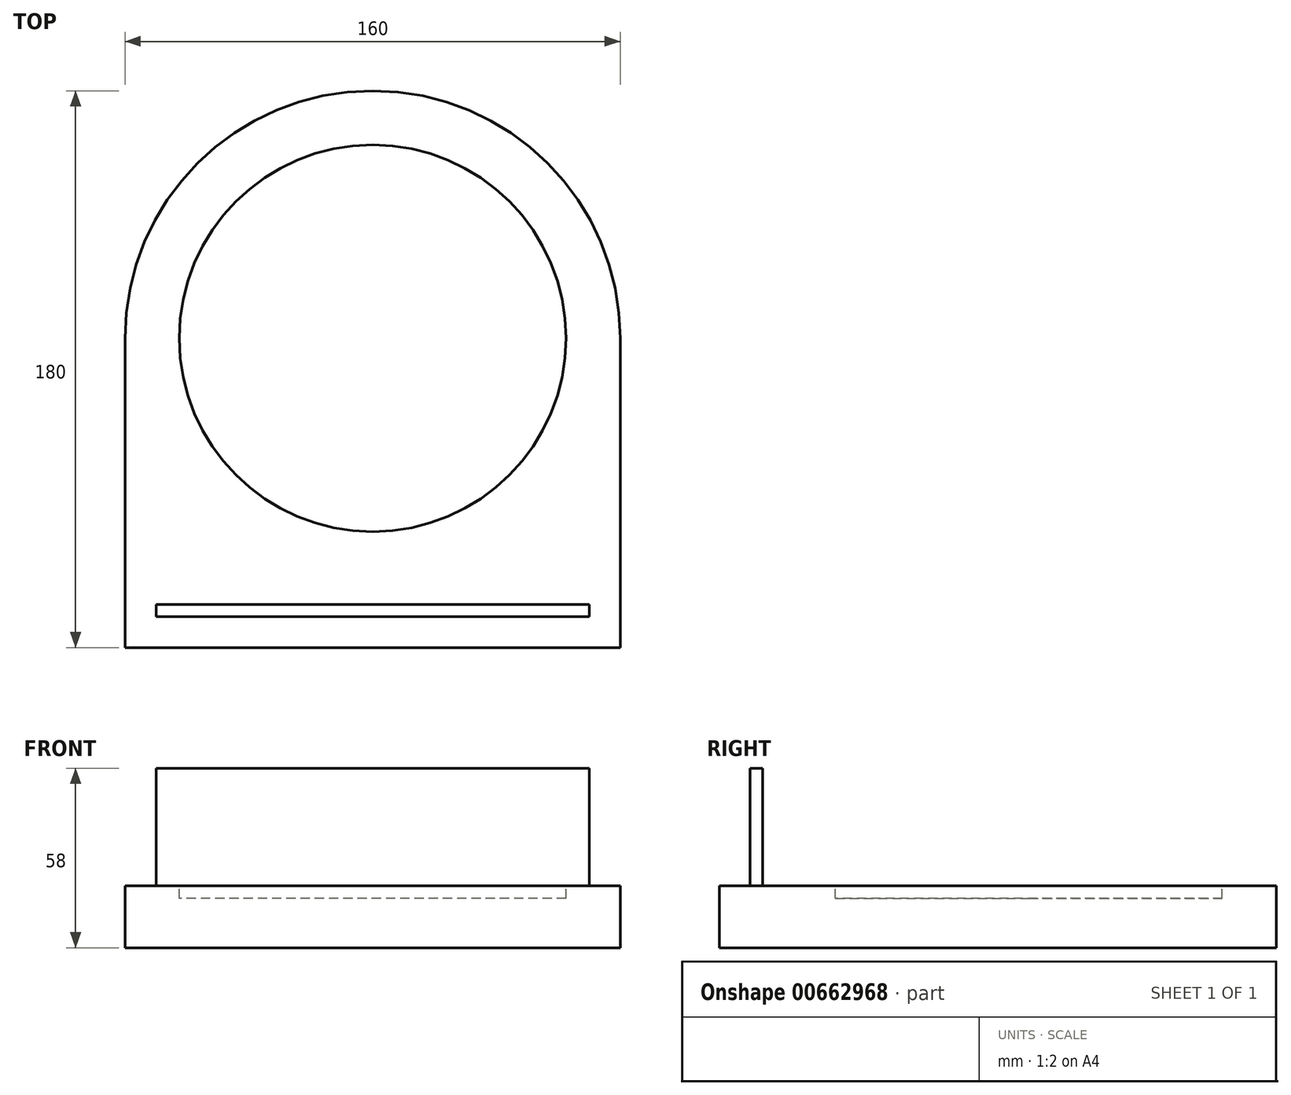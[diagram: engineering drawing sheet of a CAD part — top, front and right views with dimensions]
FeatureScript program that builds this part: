
annotation { "Feature Type Name" : "Feature", "Feature Type Description" : "" }
export const myFeature = defineFeature(function(context is Context, id is Id, definition is map)
    precondition{}
    {
        {
            var Q0;
            Q0=qCreatedBy(makeId("Top.planeOp"),FACE);
            var sketch = newSketch(context, id + "F0", { "sketchPlane" : qUnion([Q0])});
            skArc(sketch, "E0", {"start": v(80, 0) * mm, "mid": v(0, 80) * mm, "end": v(-80, 0) * mm});
            skLineSegment(sketch, "E1.top", {"start": v(-80, -100) * mm, "end": v(80, -100) * mm});
            skLineSegment(sketch, "E1.left", {"start": v(-80, 0) * mm, "end": v(-80, -100) * mm});
            skLineSegment(sketch, "E1.right", {"start": v(80, 0) * mm, "end": v(80, -100) * mm});
            skSolve(sketch);
        }
        {
            var Q0;
            Q0 = qSketchRegion(id + "F0", true);
            extrude(context, id + "F1", {"entities" : qUnion([Q0]), "depth" : 20 * mm, "offsetDistance" : 25 * mm});
        }
        {
            var Q0;
            Q0=makeQuery(id+"F1.opExtrude","CAP_FACE",FACE,{"disambiguationData":[OSD([sQuery(id+"F0.wireOp",EDGE,"E0"),sQuery(id+"F0.wireOp",EDGE,"E1.top"),sQuery(id+"F0.wireOp",EDGE,"E1.left"),sQuery(id+"F0.wireOp",EDGE,"E1.right")])],"isStart":false});
            var sketch = newSketch(context, id + "F2", { "sketchPlane" : qUnion([Q0])});
            skCircle(sketch, "E2", {"center": v(0, 0) * mm, "radius": 62.5 * mm});
            skSolve(sketch);
        }
        {
            var Q0;
            Q0=makeQuery(id+"F2.imprint","IMPRINT",FACE,{"disambiguationData":[TD([[makeQuery(id+"F2.imprint","IMPRINT",EDGE,{"derivedFrom":sQuery(id+"F2.wireOp",EDGE,"E2")}),1.0]])]});
            extrude(context, id + "F3", {"entities" : qUnion([Q0]), "operationType" : NewBodyOperationType.REMOVE, "oppositeDirection" : true, "depth" : 4 * mm, "offsetDistance" : 25 * mm});
        }
        {
            var Q0;
            Q0=makeQuery(id+"F1.opExtrude","CAP_FACE",FACE,{"disambiguationData":[OSD([sQuery(id+"F0.wireOp",EDGE,"E0"),sQuery(id+"F0.wireOp",EDGE,"E1.top"),sQuery(id+"F0.wireOp",EDGE,"E1.left"),sQuery(id+"F0.wireOp",EDGE,"E1.right")])],"isStart":false});
            var sketch = newSketch(context, id + "F4", { "sketchPlane" : qUnion([Q0])});
            skLineSegment(sketch, "E3.bottom", {"start": v(-70, -90) * mm, "end": v(70, -90) * mm});
            skLineSegment(sketch, "E3.top", {"start": v(-70, -86) * mm, "end": v(70, -86) * mm});
            skLineSegment(sketch, "E3.left", {"start": v(-70, -90) * mm, "end": v(-70, -86) * mm});
            skLineSegment(sketch, "E3.right", {"start": v(70, -90) * mm, "end": v(70, -86) * mm});
            skSolve(sketch);
        }
        {
            var Q0;
            Q0 = qSketchRegion(id + "F4", true);
            extrude(context, id + "F5", {"entities" : qUnion([Q0]), "operationType" : NewBodyOperationType.REMOVE, "oppositeDirection" : true, "depth" : 12 * mm, "offsetDistance" : 25 * mm});
        }
        {
            var Q0;
            Q0=makeQuery(id+"F5.boolean.opBoolean","COPY",FACE,{"derivedFrom":makeQuery(id+"F5.opExtrude","CAP_FACE",FACE,{"disambiguationData":[OSD([sQuery(id+"F4.wireOp",EDGE,"E3.bottom"),sQuery(id+"F4.wireOp",EDGE,"E3.top"),sQuery(id+"F4.wireOp",EDGE,"E3.left"),sQuery(id+"F4.wireOp",EDGE,"E3.right")])],"isStart":false})});
            var sketch = newSketch(context, id + "F6", { "sketchPlane" : qUnion([Q0])});
            skLineSegment(sketch, "E4.bottom", {"start": v(-70, -86) * mm, "end": v(70, -86) * mm});
            skLineSegment(sketch, "E4.top", {"start": v(-70, -90) * mm, "end": v(70, -90) * mm});
            skLineSegment(sketch, "E4.left", {"start": v(-70, -86) * mm, "end": v(-70, -90) * mm});
            skLineSegment(sketch, "E4.right", {"start": v(70, -86) * mm, "end": v(70, -90) * mm});
            skSolve(sketch);
        }
        {
            var Q0;
            Q0 = qSketchRegion(id + "F6", true);
            extrude(context, id + "F7", {"entities" : qUnion([Q0]), "operationType" : NewBodyOperationType.ADD, "depth" : 50 * mm, "offsetDistance" : 25 * mm});
        }
    });
